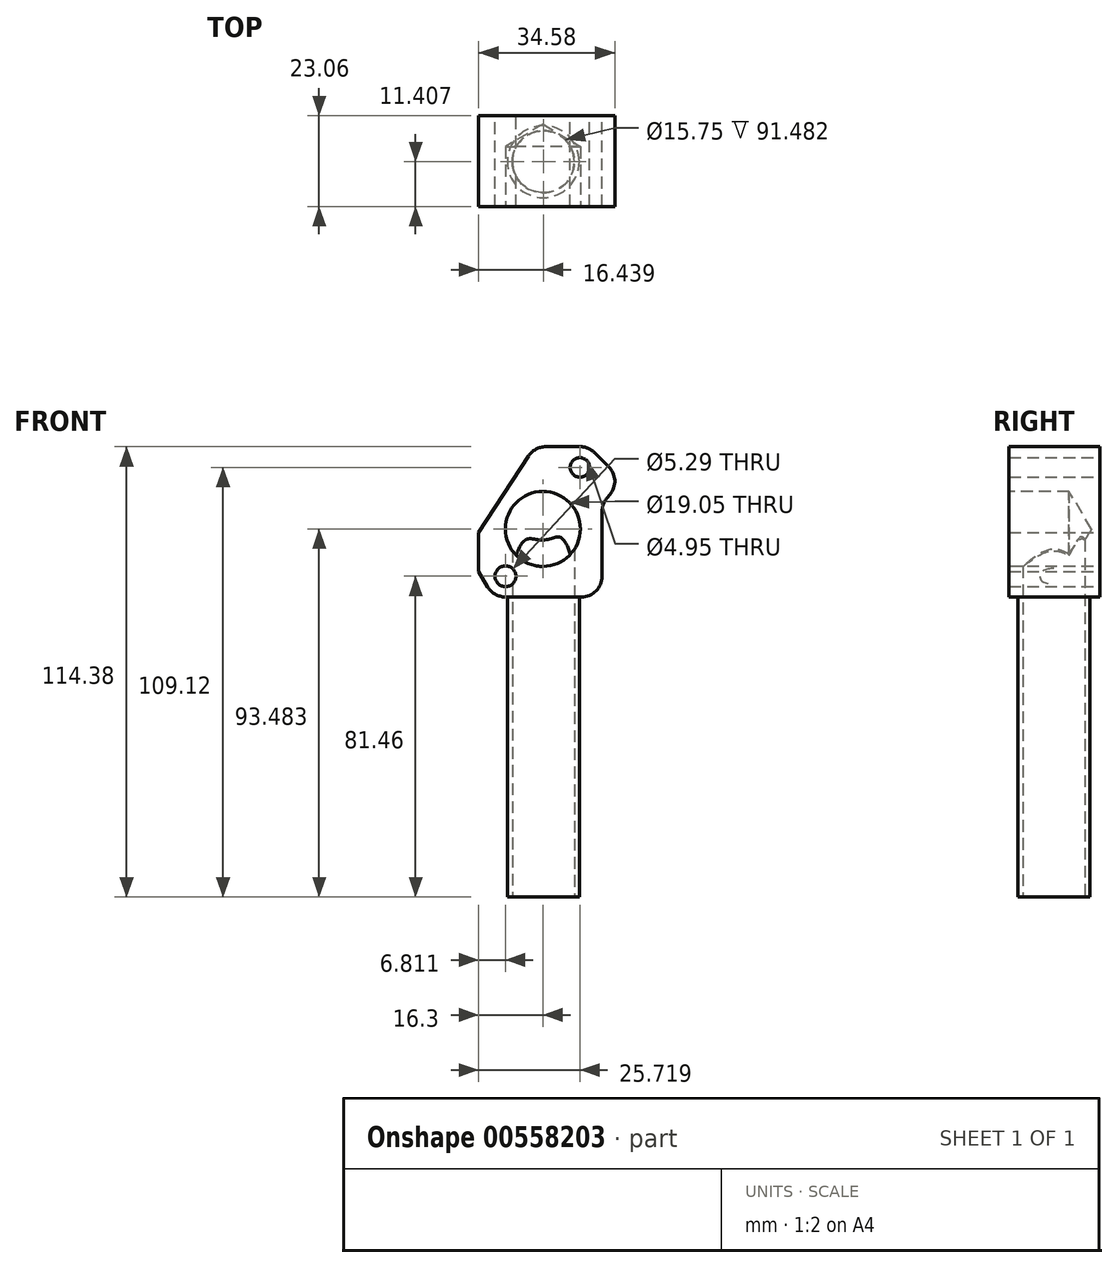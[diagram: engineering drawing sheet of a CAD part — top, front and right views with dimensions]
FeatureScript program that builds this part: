
annotation { "Feature Type Name" : "Feature", "Feature Type Description" : "" }
export const myFeature = defineFeature(function(context is Context, id is Id, definition is map)
    precondition{}
    {
        {
            var Q0;
            Q0=qCreatedBy(makeId("Front.planeOp"),FACE);
            var sketch = newSketch(context, id + "F0", { "sketchPlane" : qUnion([Q0])});
            skLineSegment(sketch, "E0.bottom", {"start": v(-8.88, 4.19) * mm, "end": v(10.43, 4.19) * mm});
            skLineSegment(sketch, "E0.top", {"start": v(1.36, 42.37) * mm, "end": v(10.03, 42.37) * mm});
            skLineSegment(sketch, "E0.left", {"start": v(-15.7, 10.6) * mm, "end": v(-15.7, 20.58) * mm});
            skLineSegment(sketch, "E0.right", {"start": v(15.69, 9.45) * mm, "end": v(15.69, 25.96) * mm});
            skLineSegment(sketch, "E1", {"start": v(-3.04, 39.98) * mm, "end": v(-15.7, 20.58) * mm});
            skLineSegment(sketch, "E2", {"start": v(-15.7, 20.58) * mm, "end": v(-15.7, 10.6) * mm});
            skLineSegment(sketch, "E3", {"start": v(-15.7, 10.6) * mm, "end": v(-13.4, 6.75) * mm});
            skLineSegment(sketch, "E4", {"start": v(13.7, 40.88) * mm, "end": v(17.3, 37.36) * mm});
            skLineSegment(sketch, "E5", {"start": v(17.63, 30.18) * mm, "end": v(16.94, 29.37) * mm});
            skArc(sketch, "E6.filletArc", {"start": v(13.7, 40.88) * mm, "mid": v(12.01, 41.98) * mm, "end": v(10.03, 42.37) * mm});
            skArc(sketch, "E7.filletArc", {"start": v(17.63, 30.18) * mm, "mid": v(18.89, 33.84) * mm, "end": v(17.3, 37.36) * mm});
            skPoint(sketch, "E8.visualSharp", {"position": v(15.69, 27.9) * mm});
            skArc(sketch, "E8.filletArc", {"start": v(16.94, 29.37) * mm, "mid": v(16.01, 27.78) * mm, "end": v(15.69, 25.96) * mm});
            skArc(sketch, "E9.filletArc", {"start": v(10.43, 4.19) * mm, "mid": v(14.15, 5.73) * mm, "end": v(15.69, 9.45) * mm});
            skArc(sketch, "E10.filletArc", {"start": v(1.36, 42.37) * mm, "mid": v(-1.14, 41.74) * mm, "end": v(-3.04, 39.98) * mm});
            skArc(sketch, "E11.filletArc", {"start": v(-13.4, 6.75) * mm, "mid": v(-11.48, 4.87) * mm, "end": v(-8.88, 4.19) * mm});
            skCircle(sketch, "E12", {"center": v(10.03, 37.11) * mm, "radius": 2.48 * mm});
            skCircle(sketch, "E13", {"center": v(-8.88, 9.45) * mm, "radius": 2.65 * mm});
            skLineSegment(sketch, "E14.bottom", {"start": v(-8.88, 4.19) * mm, "end": v(10.1, 4.19) * mm});
            skSolve(sketch);
        }
        {
            var Q0;
            Q0=makeQuery(id+"F0.imprint","IMPRINT",FACE,{"disambiguationData":[TD([[makeQuery(id+"F0.imprint","IMPRINT",EDGE,{"derivedFrom":sQuery(id+"F0.wireOp",EDGE,"E0.bottom")}),1.0]])]});
            extrude(context, id + "F1", {"entities" : qUnion([Q0]), "depth" : 23.06 * mm, "offsetDistance" : 25.4 * mm});
        }
        {
            var Q0;
            Q0=makeQuery(id+"F1.opExtrude","CAP_FACE",FACE,{"disambiguationData":[OSD([sQuery(id+"F0.wireOp",EDGE,"E0.bottom"),sQuery(id+"F0.wireOp",EDGE,"E0.top"),sQuery(id+"F0.wireOp",EDGE,"E0.right"),sQuery(id+"F0.wireOp",EDGE,"E1"),sQuery(id+"F0.wireOp",EDGE,"E2"),sQuery(id+"F0.wireOp",EDGE,"E3"),sQuery(id+"F0.wireOp",EDGE,"E4"),sQuery(id+"F0.wireOp",EDGE,"E5"),sQuery(id+"F0.wireOp",EDGE,"E6.filletArc"),sQuery(id+"F0.wireOp",EDGE,"E7.filletArc"),sQuery(id+"F0.wireOp",EDGE,"E8.filletArc"),sQuery(id+"F0.wireOp",EDGE,"E9.filletArc"),sQuery(id+"F0.wireOp",EDGE,"E10.filletArc"),sQuery(id+"F0.wireOp",EDGE,"E11.filletArc"),sQuery(id+"F0.wireOp",EDGE,"E12"),sQuery(id+"F0.wireOp",EDGE,"E13"),sQuery(id+"F0.wireOp",EDGE,"E14.bottom")])],"isStart":false});
            var sketch = newSketch(context, id + "F2", { "sketchPlane" : qUnion([Q0])});
            skCircle(sketch, "E15", {"center": v(0.61, 21.47) * mm, "radius": 9.53 * mm});
            skSolve(sketch);
        }
        {
            var Q0;
            Q0=sQuery(id+"F2.wireOp",VERTEX,"E15.center");
            var Q1;
            Q1=makeQuery(id+"F1.opExtrude","SWEPT_BODY",BODY,{"disambiguationData":[OSD([sQuery(id+"F0.wireOp",EDGE,"E0.bottom"),sQuery(id+"F0.wireOp",EDGE,"E0.top"),sQuery(id+"F0.wireOp",EDGE,"E0.right"),sQuery(id+"F0.wireOp",EDGE,"E1"),sQuery(id+"F0.wireOp",EDGE,"E2"),sQuery(id+"F0.wireOp",EDGE,"E3"),sQuery(id+"F0.wireOp",EDGE,"E4"),sQuery(id+"F0.wireOp",EDGE,"E5"),sQuery(id+"F0.wireOp",EDGE,"E6.filletArc"),sQuery(id+"F0.wireOp",EDGE,"E7.filletArc"),sQuery(id+"F0.wireOp",EDGE,"E8.filletArc"),sQuery(id+"F0.wireOp",EDGE,"E9.filletArc"),sQuery(id+"F0.wireOp",EDGE,"E10.filletArc"),sQuery(id+"F0.wireOp",EDGE,"E11.filletArc"),sQuery(id+"F0.wireOp",EDGE,"E12"),sQuery(id+"F0.wireOp",EDGE,"E13"),sQuery(id+"F0.wireOp",EDGE,"E14.bottom")])]});
            hole(context, id + "F3", {"style" : HoleStyle.SIMPLE, "endStyle" : HoleEndStyle.BLIND, "holeDiameter" : 19.05 * mm, "holeDepth" : 15.24 * mm, "isTappedThrough" : true, "tappedDepth" : 12.7 * mm, "tapClearance" : 3, "locations" : qUnion([Q0]), "scope" : qUnion([Q1])});
        }
        {
            var Q0;
            Q0=makeQuery(id+"F1.opExtrude","SWEPT_FACE",FACE,{"disambiguationData":[OSD([sQuery(id+"F0.wireOp",EDGE,"E0.bottom"),sQuery(id+"F0.wireOp",EDGE,"E14.bottom")])]});
            var sketch = newSketch(context, id + "F4", { "sketchPlane" : qUnion([Q0])});
            skLineSegment(sketch, "E16", {"start": v(0, 0) * mm, "end": v(0, 2.54) * mm});
            skCircle(sketch, "E17", {"center": v(0.75, 11.65) * mm, "radius": 9.14 * mm});
            skPoint(sketch, "E17.second.point", {"position": v(0, 20.77) * mm});
            skPoint(sketch, "E17.third.point", {"position": v(9.02, 15.55) * mm});
            skSolve(sketch);
        }
        {
            var Q0;
            Q0=sQuery(id+"F4.wireOp",VERTEX,"E17.center");
            var Q1;
            Q1=makeQuery(id+"F1.opExtrude","SWEPT_BODY",BODY,{"disambiguationData":[OSD([sQuery(id+"F0.wireOp",EDGE,"E0.bottom"),sQuery(id+"F0.wireOp",EDGE,"E0.top"),sQuery(id+"F0.wireOp",EDGE,"E0.right"),sQuery(id+"F0.wireOp",EDGE,"E1"),sQuery(id+"F0.wireOp",EDGE,"E2"),sQuery(id+"F0.wireOp",EDGE,"E3"),sQuery(id+"F0.wireOp",EDGE,"E4"),sQuery(id+"F0.wireOp",EDGE,"E5"),sQuery(id+"F0.wireOp",EDGE,"E6.filletArc"),sQuery(id+"F0.wireOp",EDGE,"E7.filletArc"),sQuery(id+"F0.wireOp",EDGE,"E8.filletArc"),sQuery(id+"F0.wireOp",EDGE,"E9.filletArc"),sQuery(id+"F0.wireOp",EDGE,"E10.filletArc"),sQuery(id+"F0.wireOp",EDGE,"E11.filletArc"),sQuery(id+"F0.wireOp",EDGE,"E12"),sQuery(id+"F0.wireOp",EDGE,"E13"),sQuery(id+"F0.wireOp",EDGE,"E14.bottom")])]});
            hole(context, id + "F5", {"style" : HoleStyle.SIMPLE, "endStyle" : HoleEndStyle.BLIND, "holeDiameter" : 15.75 * mm, "holeDepth" : 17.78 * mm, "isTappedThrough" : true, "tappedDepth" : 12.7 * mm, "tapClearance" : 3, "locations" : qUnion([Q0]), "scope" : qUnion([Q1])});
        }
        {
            var Q0;
            Q0=makeQuery(id+"F4.imprint","IMPRINT",FACE,{"disambiguationData":[TD([[makeQuery(id+"F4.imprint","IMPRINT",EDGE,{"derivedFrom":sQuery(id+"F4.wireOp",EDGE,"E17")}),1.0]])]});
            extrude(context, id + "F6", {"entities" : qUnion([Q0]), "operationType" : NewBodyOperationType.ADD, "depth" : 76.2 * mm, "offsetDistance" : 25.4 * mm});
        }
        {
            var Q0;
            Q0=sQuery(id+"F4.wireOp",VERTEX,"E17.center");
            var Q1;
            Q1=makeQuery(id+"F1.opExtrude","SWEPT_BODY",BODY,{"disambiguationData":[OSD([sQuery(id+"F0.wireOp",EDGE,"E0.bottom"),sQuery(id+"F0.wireOp",EDGE,"E0.top"),sQuery(id+"F0.wireOp",EDGE,"E0.right"),sQuery(id+"F0.wireOp",EDGE,"E1"),sQuery(id+"F0.wireOp",EDGE,"E2"),sQuery(id+"F0.wireOp",EDGE,"E3"),sQuery(id+"F0.wireOp",EDGE,"E4"),sQuery(id+"F0.wireOp",EDGE,"E5"),sQuery(id+"F0.wireOp",EDGE,"E6.filletArc"),sQuery(id+"F0.wireOp",EDGE,"E7.filletArc"),sQuery(id+"F0.wireOp",EDGE,"E8.filletArc"),sQuery(id+"F0.wireOp",EDGE,"E9.filletArc"),sQuery(id+"F0.wireOp",EDGE,"E10.filletArc"),sQuery(id+"F0.wireOp",EDGE,"E11.filletArc"),sQuery(id+"F0.wireOp",EDGE,"E12"),sQuery(id+"F0.wireOp",EDGE,"E13"),sQuery(id+"F0.wireOp",EDGE,"E14.bottom")])]});
            hole(context, id + "F7", {"style" : HoleStyle.SIMPLE, "endStyle" : HoleEndStyle.BLIND, "oppositeDirection" : true, "holeDiameter" : 15.75 * mm, "holeDepth" : 78.74 * mm, "isTappedThrough" : true, "tappedDepth" : 12.7 * mm, "tapClearance" : 3, "locations" : qUnion([Q0]), "scope" : qUnion([Q1])});
        }
    });
